# Revit family: POLAR plus Gleitlager U140 Ø323
name_source: partatom
category: HLS-Bauteile
units: mm (PartAtom-declared; Revit-internal decimal feet)

## family parameters
Arbeitsebenenbasiert = Ja
Beim Laden mit Abzugskörper schneiden = Nein
Bemaßung runder Anschluss = Durchmesser verwenden
Beschriftungsausrichtung beibehalten = Nein
Gemeinsam genutzt = Ja
Immer vertikal = Nein
Klassifizierung = Keine
Raumberechnungspunkt = Nein
Teiletyp = Normal

## types (1)
- POLAR plus Gleitlager U140 Ø323
    Artikelnummer = 74742324
    Breite = 427 mm
    Breite Material = 50 mm
    Breite Unterbau = 140 mm
    Dämmstärke = 40 mm  [stored 0.131234 ft]
    EAN = 4250928443045
    Fabrikat = MEFA
    Gewicht = 11,05 kg
    Gewicht pro Bauteil = 11,05 kg
    Höhe Sohle = 96 mm
    Höhe Unterbau = 60 mm
    Kurztext1 = Gleitlager U Polar Plus
    Kurztext2 = 323,9 mm Iso 40 x 226 mm
    Länge Schale = 226 mm
    Länge Unterbau = 220 mm
    Material = Stahl
    Materialname = S235
    Mengeneinheit = St
    Rohraußendurchmesser = 324 mm
    Stärke Material = 5 mm  [stored 0.0164042 ft]
    Vorgabe-Ansicht = 1219 mm
    vpe = 1

note: [stored X ft] marks values corroborated as IEEE doubles in the binary element streams (Revit-internal decimal feet)

## geometry (parser evidence)
native form markers: Sweep x6
no freeform markers — native parametric forms only
